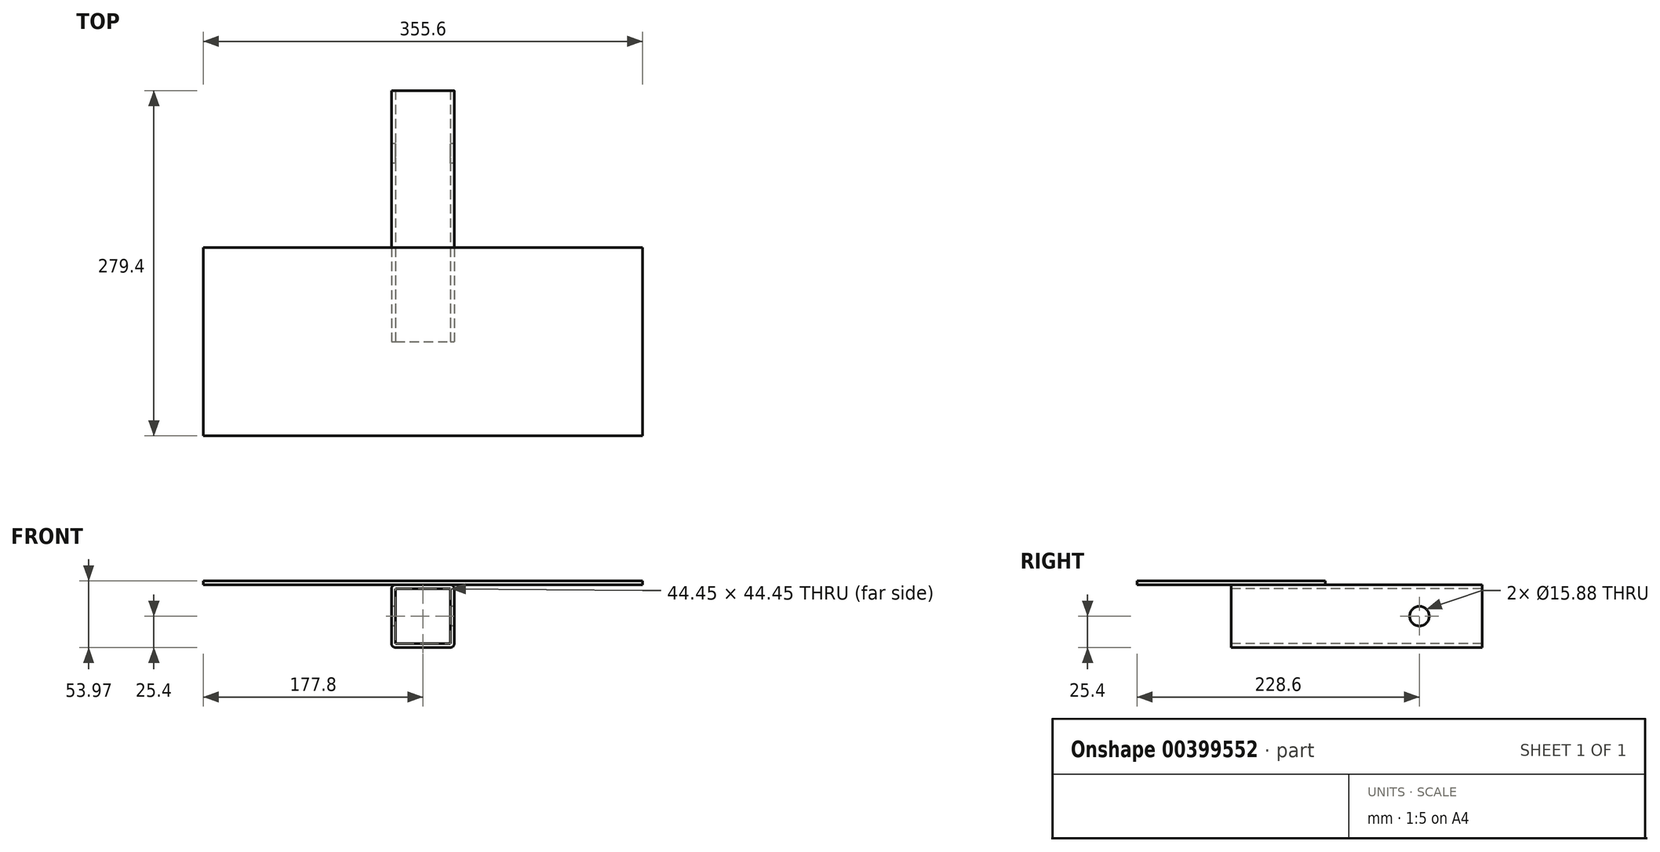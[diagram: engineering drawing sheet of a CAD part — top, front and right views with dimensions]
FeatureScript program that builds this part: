
annotation { "Feature Type Name" : "Feature", "Feature Type Description" : "" }
export const myFeature = defineFeature(function(context is Context, id is Id, definition is map)
    precondition{}
    {
        {
            var Q0;
            Q0=qCreatedBy(makeId("Top.planeOp"),FACE);
            var sketch = newSketch(context, id + "F0", { "sketchPlane" : qUnion([Q0])});
            skLineSegment(sketch, "E0.bottom", {"start": v(177.8, 76.2) * mm, "end": v(-177.8, 76.2) * mm});
            skLineSegment(sketch, "E0.top", {"start": v(177.8, -76.2) * mm, "end": v(-177.8, -76.2) * mm});
            skLineSegment(sketch, "E0.left", {"start": v(177.8, 76.2) * mm, "end": v(177.8, -76.2) * mm});
            skLineSegment(sketch, "E0.right", {"start": v(-177.8, 76.2) * mm, "end": v(-177.8, -76.2) * mm});
            skPoint(sketch, "E0.middle", {"position": v(0, 0) * mm});
            skSolve(sketch);
        }
        {
            var Q0;
            Q0=makeQuery(id+"F0.imprint","IMPRINT",FACE,{"disambiguationData":[TD([[makeQuery(id+"F0.imprint","IMPRINT",EDGE,{"derivedFrom":sQuery(id+"F0.wireOp",EDGE,"E0.bottom")}),1.0]])]});
            extrude(context, id + "F1", {"entities" : qUnion([Q0]), "depth" : 3.17 * mm});
        }
        {
            var Q0;
            Q0=qCreatedBy(makeId("Front.planeOp"),FACE);
            var sketch = newSketch(context, id + "F2", { "sketchPlane" : qUnion([Q0])});
            skLineSegment(sketch, "E1", {"start": v(0, 0) * mm, "end": v(0, -50.8) * mm, "construction": true});
            skLineSegment(sketch, "E2.bottom", {"start": v(-22.23, 0) * mm, "end": v(22.23, 0) * mm});
            skLineSegment(sketch, "E2.top", {"start": v(-22.23, -50.8) * mm, "end": v(22.23, -50.8) * mm});
            skLineSegment(sketch, "E2.left", {"start": v(-25.4, -3.18) * mm, "end": v(-25.4, -47.62) * mm});
            skLineSegment(sketch, "E2.right", {"start": v(25.4, -3.17) * mm, "end": v(25.4, -47.63) * mm});
            skPoint(sketch, "E2.middle", {"position": v(0, -25.4) * mm});
            skLineSegment(sketch, "E3.0", {"start": v(-22.23, -3.18) * mm, "end": v(-22.23, -47.62) * mm});
            skLineSegment(sketch, "E3.1", {"start": v(-22.23, -3.18) * mm, "end": v(22.23, -3.18) * mm});
            skLineSegment(sketch, "E3.2", {"start": v(22.23, -3.18) * mm, "end": v(22.23, -47.62) * mm});
            skLineSegment(sketch, "E3.3", {"start": v(-22.23, -47.62) * mm, "end": v(22.23, -47.62) * mm});
            skPoint(sketch, "E4.visualSharp", {"position": v(-25.4, 0) * mm});
            skArc(sketch, "E4.filletArc", {"start": v(-22.23, 0) * mm, "mid": v(-24.47, -0.93) * mm, "end": v(-25.4, -3.18) * mm});
            skPoint(sketch, "E5.visualSharp", {"position": v(-25.4, -50.8) * mm});
            skArc(sketch, "E5.filletArc", {"start": v(-25.4, -47.62) * mm, "mid": v(-24.47, -49.87) * mm, "end": v(-22.23, -50.8) * mm});
            skPoint(sketch, "E6.visualSharp", {"position": v(25.4, -50.8) * mm});
            skArc(sketch, "E6.filletArc", {"start": v(22.23, -50.8) * mm, "mid": v(24.47, -49.87) * mm, "end": v(25.4, -47.63) * mm});
            skPoint(sketch, "E7.visualSharp", {"position": v(25.4, 0) * mm});
            skArc(sketch, "E7.filletArc", {"start": v(25.4, -3.17) * mm, "mid": v(24.47, -0.93) * mm, "end": v(22.23, 0) * mm});
            skSolve(sketch);
        }
        {
            var Q0;
            Q0=makeQuery(id+"F2.imprint","IMPRINT",FACE,{"disambiguationData":[TD([[makeQuery(id+"F2.imprint","IMPRINT",EDGE,{"derivedFrom":sQuery(id+"F2.wireOp",EDGE,"E2.bottom")}),-1.0]])]});
            extrude(context, id + "F3", {"entities" : qUnion([Q0]), "operationType" : NewBodyOperationType.ADD, "oppositeDirection" : true, "depth" : 203.2 * mm});
        }
        {
            var Q0;
            Q0=makeQuery(id+"F3.opExtrude","SWEPT_FACE",FACE,{"disambiguationData":[OSD([sQuery(id+"F2.wireOp",EDGE,"E2.left")])]});
            var sketch = newSketch(context, id + "F4", { "sketchPlane" : qUnion([Q0])});
            skPoint(sketch, "E8.0", {"position": v(-76.2, 0) * mm});
            skPoint(sketch, "E9.0", {"position": v(0, -25.4) * mm});
            skLineSegment(sketch, "E10", {"start": v(-76.2, -25.4) * mm, "end": v(-152.4, -25.4) * mm});
            skSolve(sketch);
        }
        {
            var Q0;
            Q0=sQuery(id+"F4.wireOp",VERTEX,"E10.end");
            var Q1;
            Q1=makeQuery(id+"F1.opExtrude","SWEPT_BODY",BODY,{"disambiguationData":[OSD([sQuery(id+"F0.wireOp",EDGE,"E0.bottom"),sQuery(id+"F0.wireOp",EDGE,"E0.top"),sQuery(id+"F0.wireOp",EDGE,"E0.left"),sQuery(id+"F0.wireOp",EDGE,"E0.right")])]});
            hole(context, id + "F5", {"style" : HoleStyle.SIMPLE, "endStyle" : HoleEndStyle.THROUGH, "holeDiameter" : 15.88 * mm, "locations" : qUnion([Q0]), "scope" : qUnion([Q1]), "isTappedThrough" : true});
        }
    });
